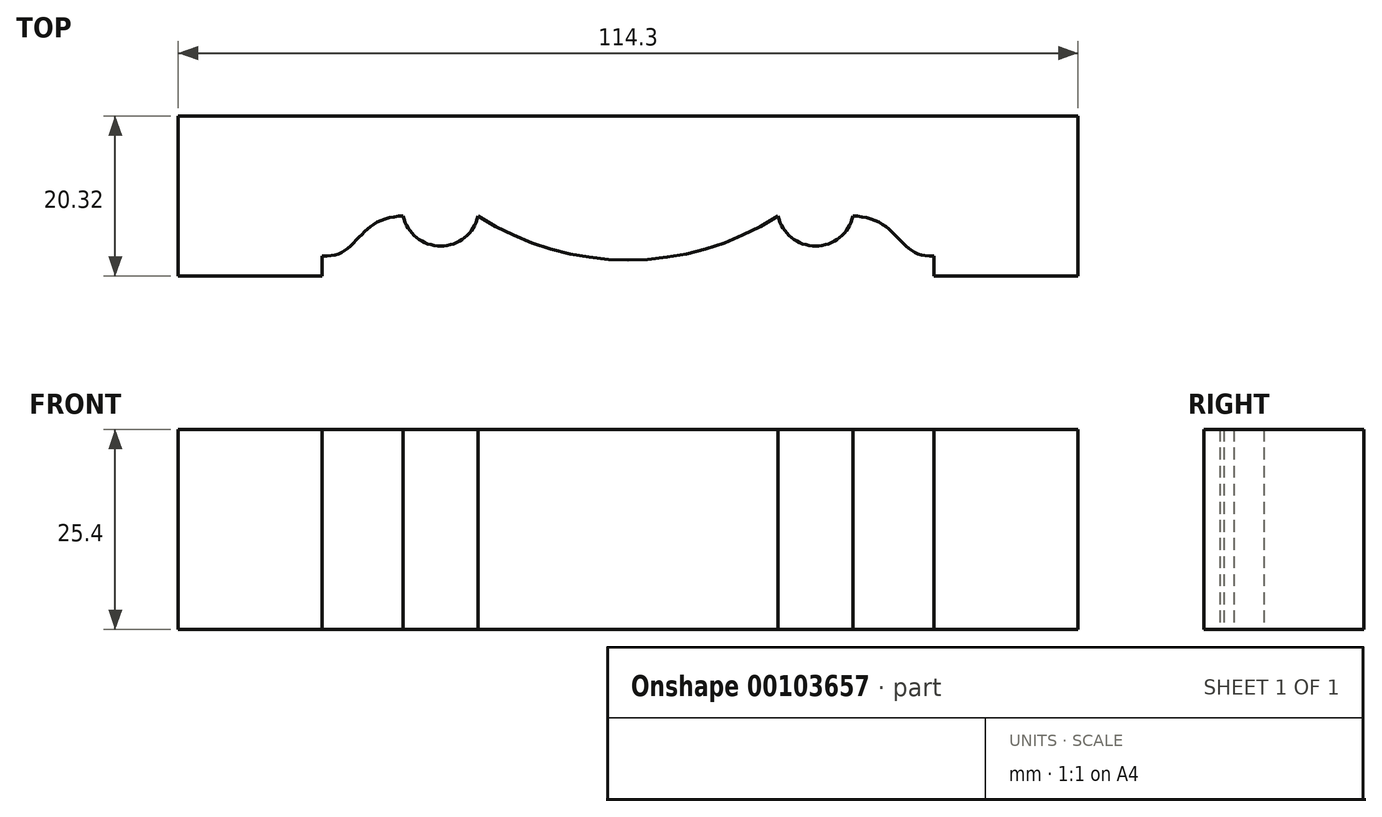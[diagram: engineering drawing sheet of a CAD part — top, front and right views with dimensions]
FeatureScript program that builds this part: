
annotation { "Feature Type Name" : "Feature", "Feature Type Description" : "" }
export const myFeature = defineFeature(function(context is Context, id is Id, definition is map)
    precondition{}
    {
        {
            var Q0;
            Q0=qCreatedBy(makeId("Top.planeOp"),FACE);
            var sketch = newSketch(context, id + "F0", { "sketchPlane" : qUnion([Q0])});
            skLineSegment(sketch, "E0.bottom", {"start": v(0, 0) * mm, "end": v(57.15, 0) * mm});
            skLineSegment(sketch, "E0.left", {"start": v(0, 0) * mm, "end": v(0, -20.32) * mm});
            skLineSegment(sketch, "E1", {"start": v(0, -20.32) * mm, "end": v(18.29, -20.32) * mm});
            skLineSegment(sketch, "E2", {"start": v(18.29, -20.32) * mm, "end": v(18.29, -17.78) * mm});
            skLineSegment(sketch, "E3", {"start": v(28.57, 0) * mm, "end": v(28.58, -12.7) * mm, "construction": true});
            skLineSegment(sketch, "E4", {"start": v(28.58, -12.7) * mm, "end": v(38.1, -12.7) * mm, "construction": true});
            skArc(sketch, "E5", {"start": v(28.58, -12.7) * mm, "mid": v(33.34, -16.51) * mm, "end": v(38.1, -12.7) * mm});
            skLineSegment(sketch, "E6", {"start": v(57.15, 0) * mm, "end": v(57.15, -18.29) * mm});
            skFitSpline(sketch, "E7", {"points": [v(18.29, -17.78) * mm, v(20.93, -17.2) * mm, v(23.02, -15.35) * mm, v(25.15, -13.57) * mm, v(28.58, -12.7) * mm], "startDerivative": vector(15.17, 0) * mm, "endDerivative": vector(13.23, 0) * mm});
            skArc(sketch, "E8", {"start": v(38.1, -12.7) * mm, "mid": v(47.22, -16.86) * mm, "end": v(57.15, -18.29) * mm});
            skPoint(sketch, "E9.orphan", {"position": v(76.2, -12.7) * mm});
            skSolve(sketch);
        }
        {
            var Q0;
            Q0=makeQuery(id+"F0.imprint","IMPRINT",FACE,{"disambiguationData":[TD([[makeQuery(id+"F0.imprint","IMPRINT",EDGE,{"derivedFrom":sQuery(id+"F0.wireOp",EDGE,"E0.bottom")}),-1.0]])]});
            extrude(context, id + "F1", {"entities" : qUnion([Q0]), "depth" : 25.4 * mm});
        }
        {
            var Q0;
            Q0=makeQuery(id+"F1.opExtrude","SWEPT_BODY",BODY,{"disambiguationData":[OSD([sQuery(id+"F0.wireOp",EDGE,"E0.bottom"),sQuery(id+"F0.wireOp",EDGE,"E0.left"),sQuery(id+"F0.wireOp",EDGE,"E1"),sQuery(id+"F0.wireOp",EDGE,"E2"),sQuery(id+"F0.wireOp",EDGE,"E5"),sQuery(id+"F0.wireOp",EDGE,"E6"),sQuery(id+"F0.wireOp",EDGE,"E7"),sQuery(id+"F0.wireOp",EDGE,"E8")])]});
            var Q1;
            Q1=makeQuery(id+"F1.opExtrude","SWEPT_FACE",FACE,{"disambiguationData":[OSD([sQuery(id+"F0.wireOp",EDGE,"E6")])]});
            mirror(context, id + "F2", {"operationType" : NewBodyOperationType.ADD, "entities" : qUnion([Q0]), "mirrorPlane" : qUnion([Q1])});
        }
    });
